# Revit family: Faucet-Lavatory-KOHLER-SINGULIER-K-10860IN_1
name_source: partatom
category: Plumbing Fixtures
revit_build: Autodesk Revit 2017 (Build: 20160225_1515(x64)
units: mm (PartAtom-declared; Revit-internal decimal feet)

## family parameters
Cut with Voids When Loaded = No
Host = Face
OmniClass Number = 23.31.11.00
OmniClass Title = Faucets
Part Type = Normal
Room Calculation Point = No
Round Connector Dimension = Use Diameter
Shared = No

## types (3) — shared parameters
ADA Compliant = No
Assembly Code = D2010
CW Connection = Yes
Cold Water Inlet = Cold Water Inlet
Date Modified = 07/16/2020
Default Elevation = 36"
Description = Lever basin mixer tap
Flow Rate = 1 GPM
HW Connection = Yes
Handle Clearance = 3 3/8"
Height = 7 1/16"
Hot Water Inlet = Hot Water Inlet
Length = 3 15/16"
Manufacturer = KOHLER Co.
Master Format 2014 Name = Residential Faucets, Supplies, and Trim
MasterFormat 2014 = 22.41.39
Material = Solid Brass Construction
Pressure = 60.00 psi
Product Name = SINGULIER
Spout Reach = 3 15/16"
URL = https://www.kohler.co.in
Vent Connection = No
Waste Connection = No
Waste Water Outlet = Waste Water Outlet
WaterSense Certified = No
Width = 1 7/8"
zero-valued in all types: WFU

## per-type parameters (varying)
| type | Drain Included | Finish | Model | Type |
| CP-Polished Chrome | Yes | Kohler-Metal-CP-Polished_Chrome | K-10860IN-4-CP | 1 |
| No Drain, CP-Polished Chrome | No | Kohler-Metal-CP-Polished_Chrome | K-10860IN-4ND-CP | 2 |
| No Drain, AF-Vibrant French Gold | No | Kohler-Metal-AF-Vibrant_French_Gold | K-10860IN-4ND-AF | 3 |

## geometry (parser evidence)
native form markers: Sweep x6
no freeform markers — native parametric forms only
